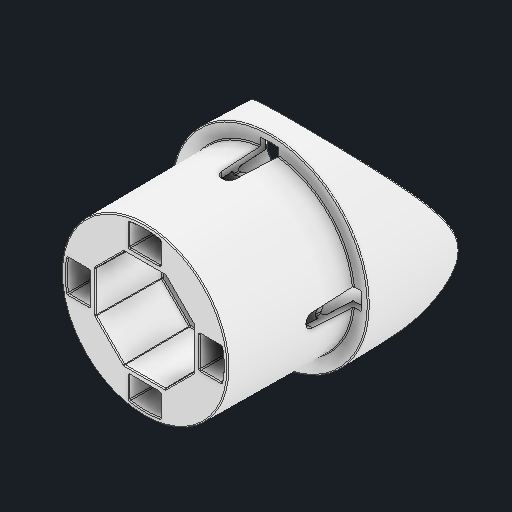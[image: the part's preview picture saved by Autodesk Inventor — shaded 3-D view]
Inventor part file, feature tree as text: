
AUTODESK INVENTOR PART (.ipt)
format: ipt  version: 2024 (Build 280153000, 153)  size: 2,301,440 bytes
history: native  units: in
note: dims shown in document units (in); Inventor stores cm internally (conversion verified against a paired STEP export)
features: fillet x1
ambient origin geometry x8: Origin, YZ Plane, XZ Plane, XY Plane, X Axis, Y Axis, Z Axis, Center Point
bodies: Solid1 (feature_tree)
feature tree (1):
  fillet  "Fillet9"  [1 undecoded]
note: 1 required parameter value undecoded (feature->parameter linkage not recoverable at this tier; creation-order binding heuristic only, values carry confidence <= 0.55)
